# Revit family: WAP-Enclosure_Indoor_Ventev_2x2x1-5in-Bevel-CTEN
name_source: partatom
category: Generic Models
units: mm (PartAtom-declared; Revit-internal decimal feet)

## family parameters
Can host rebar = No
Classification Number = 23.85.50.00
Cut with Voids When Loaded = No
Host = Face
Maintain Annotation Orientation = No
Part Type = Normal
Room Calculation Point = No
Round Connector Dimension = Use Diameter
Shared = No

## types (3) — shared parameters
Accent Material = Plastic - Ventev - White
Assembly Code = D5030600
Construction Details = http://www.arcat.com
Default Elevation = 0' - 0"
Keynote = 27 20 00
Manufacturer = Ventev Innovations
Manufacturer Website = http://www.terra-wave.com
Product Data = http://www.arcat.com
Revision = R1_2016-12
Sales Information = http://www.terra-wave.com
Standards Conformance = NEC300-22 and 300-23
URL = http://www.terra-wave.com
Unit Depth = 0' - 1 1/2"
Unit Length = 2' - 0"
Unit Width = 2' - 0"
zero-valued in all types: Expected Lifespan (Years), Maintenance Schedule (Months), Warranty Duration (Years)

## per-type parameters (varying)
| type | Description | Door Design | Model |
| Aruba 225 | Ventev Beveled Ceiling Tile WAP Enclosure - TW-CTEN-2x2-225B as Specified | CTENDoor_Aruba205-215-225 | TW-CTEN-2X2-225B |
| Aruba 205 | Ventev Beveled Ceiling Tile WAP Enclosure - TW-CTEN-2x2-205B as Specified | CTENDoor_Aruba205-215-225 | TW-CTEN-2X2-205B |
| CISCO 1142 3500 3600 3700 | Ventev Beveled Ceiling Tile WAP Enclosure - TW-CTEN-2x2-1142B as Specified | CTENDoor_CISCO1142-2600-3500-3600 | TW-CTEN-2X2-1142B |

## geometry (parser evidence)
native form markers: Sweep x6
no freeform markers — native parametric forms only
